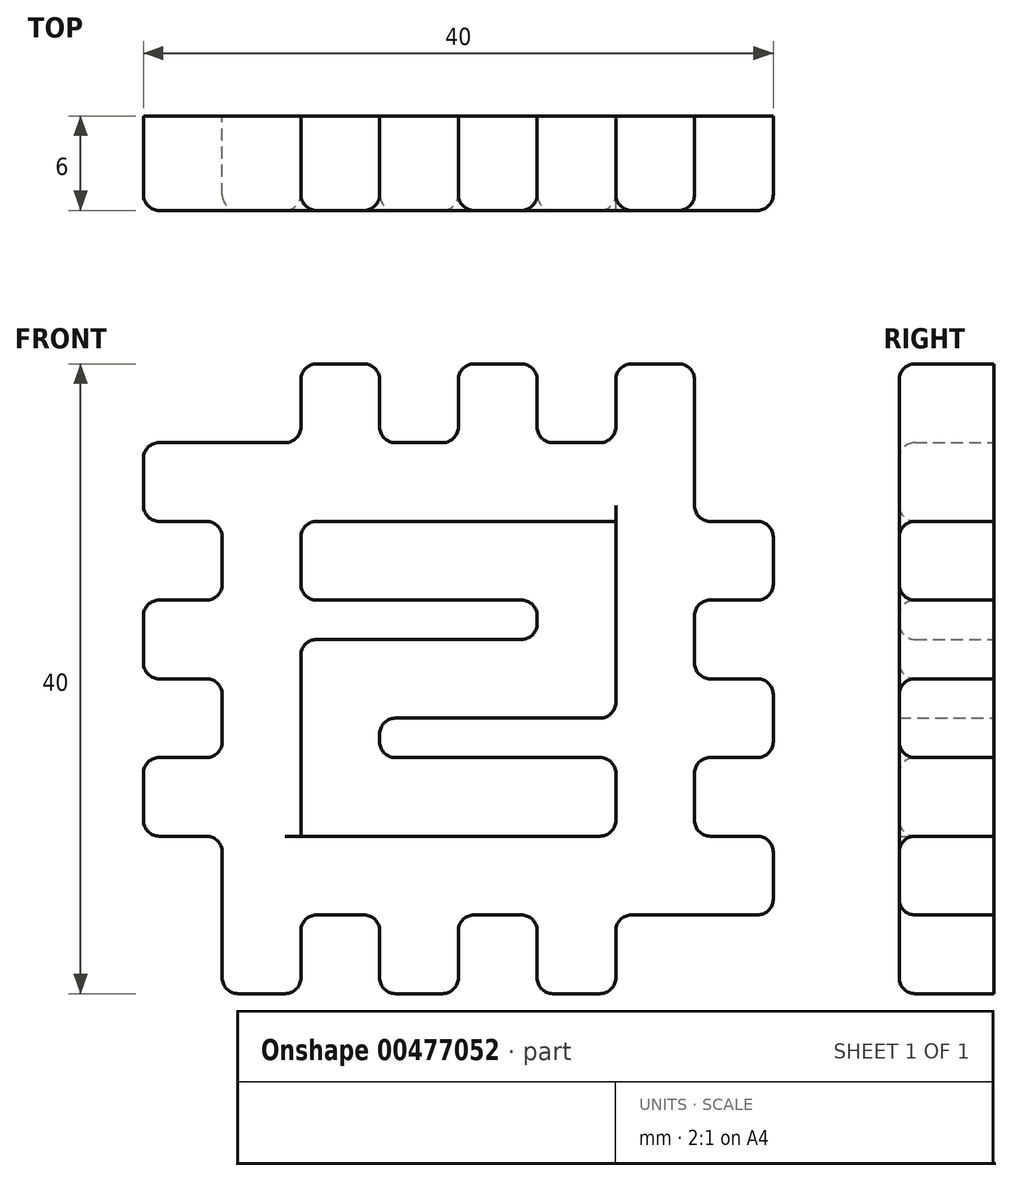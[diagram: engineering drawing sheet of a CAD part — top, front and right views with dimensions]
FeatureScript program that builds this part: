
annotation { "Feature Type Name" : "Feature", "Feature Type Description" : "" }
export const myFeature = defineFeature(function(context is Context, id is Id, definition is map)
    precondition{}
    {
        {
            var Q0;
            Q0=qCreatedBy(makeId("Front.planeOp"),FACE);
            var sketch = newSketch(context, id + "F0", { "sketchPlane" : qUnion([Q0])});
            skLineSegment(sketch, "E0.bottom", {"start": v(-15, -15) * mm, "end": v(15, -15) * mm});
            skLineSegment(sketch, "E0.top", {"start": v(-15, 15) * mm, "end": v(15, 15) * mm});
            skLineSegment(sketch, "E0.left", {"start": v(-15, -15) * mm, "end": v(-15, 15) * mm});
            skLineSegment(sketch, "E0.right", {"start": v(15, -15) * mm, "end": v(15, 15) * mm});
            skPoint(sketch, "E0.middle", {"position": v(0, 0) * mm});
            skLineSegment(sketch, "E1.bottom", {"start": v(-15, 15) * mm, "end": v(-20, 15) * mm});
            skLineSegment(sketch, "E1.top", {"start": v(-15, 10) * mm, "end": v(-20, 10) * mm});
            skLineSegment(sketch, "E1.left", {"start": v(-15, 15) * mm, "end": v(-15, 10) * mm});
            skLineSegment(sketch, "E1.right", {"start": v(-20, 15) * mm, "end": v(-20, 10) * mm});
            skPoint(sketch, "E2", {"position": v(-15, 0) * mm});
            skPoint(sketch, "E3", {"position": v(0, 15) * mm});
            skPoint(sketch, "E4", {"position": v(15, 0) * mm});
            skPoint(sketch, "E5", {"position": v(0, -15) * mm});
            skLineSegment(sketch, "E6.bottom", {"start": v(-15, 0) * mm, "end": v(-20, 0) * mm});
            skLineSegment(sketch, "E6.top", {"start": v(-15, 5) * mm, "end": v(-20, 5) * mm});
            skLineSegment(sketch, "E6.left", {"start": v(-15, 0) * mm, "end": v(-15, 5) * mm});
            skLineSegment(sketch, "E6.right", {"start": v(-20, 0) * mm, "end": v(-20, 5) * mm});
            skPoint(sketch, "E7", {"position": v(-15, -7.74) * mm});
            skPoint(sketch, "E8", {"position": v(-7.28, -15) * mm});
            skPoint(sketch, "E9", {"position": v(7.64, -15) * mm});
            skPoint(sketch, "E10", {"position": v(15, -7.4) * mm});
            skPoint(sketch, "E11", {"position": v(15, 8.08) * mm});
            skPoint(sketch, "E12", {"position": v(7.83, 15) * mm});
            skPoint(sketch, "E13", {"position": v(-7.7, 15) * mm});
            skPoint(sketch, "E14", {"position": v(-15, -5) * mm});
            skPoint(sketch, "E15", {"position": v(-15, -11.17) * mm});
            skPoint(sketch, "E16", {"position": v(-11.04, -15) * mm});
            skPoint(sketch, "E17", {"position": v(-3.27, -15) * mm});
            skPoint(sketch, "E18", {"position": v(5, -15) * mm});
            skPoint(sketch, "E19", {"position": v(11.4, -15) * mm});
            skPoint(sketch, "E20", {"position": v(15, -11.1) * mm});
            skPoint(sketch, "E21", {"position": v(15, -3.78) * mm});
            skPoint(sketch, "E22", {"position": v(15, 3.83) * mm});
            skPoint(sketch, "E23", {"position": v(15, 10) * mm});
            skPoint(sketch, "E24", {"position": v(11.09, 15) * mm});
            skPoint(sketch, "E25", {"position": v(4.04, 15) * mm});
            skPoint(sketch, "E26", {"position": v(-3.6, 15) * mm});
            skPoint(sketch, "E27", {"position": v(-11.54, 15) * mm});
            skLineSegment(sketch, "E28.bottom", {"start": v(-15, -5) * mm, "end": v(-20, -5) * mm});
            skLineSegment(sketch, "E28.top", {"start": v(-15, -10) * mm, "end": v(-20, -10) * mm});
            skLineSegment(sketch, "E28.left", {"start": v(-15, -5) * mm, "end": v(-15, -10) * mm});
            skLineSegment(sketch, "E28.right", {"start": v(-20, -5) * mm, "end": v(-20, -10) * mm});
            skLineSegment(sketch, "E29.bottom", {"start": v(15, 10) * mm, "end": v(20, 10) * mm});
            skLineSegment(sketch, "E29.top", {"start": v(15, 5) * mm, "end": v(20, 5) * mm});
            skLineSegment(sketch, "E29.left", {"start": v(15, 10) * mm, "end": v(15, 5) * mm});
            skLineSegment(sketch, "E29.right", {"start": v(20, 10) * mm, "end": v(20, 5) * mm});
            skLineSegment(sketch, "E30.bottom", {"start": v(15, 0) * mm, "end": v(20, 0) * mm});
            skLineSegment(sketch, "E30.top", {"start": v(15, -5) * mm, "end": v(20, -5) * mm});
            skLineSegment(sketch, "E30.left", {"start": v(15, 0) * mm, "end": v(15, -5) * mm});
            skLineSegment(sketch, "E30.right", {"start": v(20, 0) * mm, "end": v(20, -5) * mm});
            skLineSegment(sketch, "E31.bottom", {"start": v(15, -15) * mm, "end": v(20, -15) * mm});
            skLineSegment(sketch, "E31.top", {"start": v(15, -10) * mm, "end": v(20, -10) * mm});
            skLineSegment(sketch, "E31.left", {"start": v(15, -15) * mm, "end": v(15, -10) * mm});
            skLineSegment(sketch, "E31.right", {"start": v(20, -15) * mm, "end": v(20, -10) * mm});
            skLineSegment(sketch, "E32.bottom", {"start": v(-15, -15) * mm, "end": v(-10, -15) * mm});
            skLineSegment(sketch, "E32.top", {"start": v(-15, -20) * mm, "end": v(-10, -20) * mm});
            skLineSegment(sketch, "E32.left", {"start": v(-15, -15) * mm, "end": v(-15, -20) * mm});
            skLineSegment(sketch, "E32.right", {"start": v(-10, -15) * mm, "end": v(-10, -20) * mm});
            skLineSegment(sketch, "E33.bottom", {"start": v(0, -15) * mm, "end": v(-5, -15) * mm});
            skLineSegment(sketch, "E33.top", {"start": v(0, -20) * mm, "end": v(-5, -20) * mm});
            skLineSegment(sketch, "E33.left", {"start": v(0, -15) * mm, "end": v(0, -20) * mm});
            skLineSegment(sketch, "E33.right", {"start": v(-5, -15) * mm, "end": v(-5, -20) * mm});
            skLineSegment(sketch, "E34.bottom", {"start": v(5, -15) * mm, "end": v(10, -15) * mm});
            skLineSegment(sketch, "E34.top", {"start": v(5, -20) * mm, "end": v(10, -20) * mm});
            skLineSegment(sketch, "E34.left", {"start": v(5, -15) * mm, "end": v(5, -20) * mm});
            skLineSegment(sketch, "E34.right", {"start": v(10, -15) * mm, "end": v(10, -20) * mm});
            skLineSegment(sketch, "E35.bottom", {"start": v(-10, 15) * mm, "end": v(-5, 15) * mm});
            skLineSegment(sketch, "E35.top", {"start": v(-10, 20) * mm, "end": v(-5, 20) * mm});
            skLineSegment(sketch, "E35.left", {"start": v(-10, 15) * mm, "end": v(-10, 20) * mm});
            skLineSegment(sketch, "E35.right", {"start": v(-5, 15) * mm, "end": v(-5, 20) * mm});
            skLineSegment(sketch, "E36.bottom", {"start": v(0, 15) * mm, "end": v(5, 15) * mm});
            skLineSegment(sketch, "E36.top", {"start": v(0, 20) * mm, "end": v(5, 20) * mm});
            skLineSegment(sketch, "E36.left", {"start": v(0, 15) * mm, "end": v(0, 20) * mm});
            skLineSegment(sketch, "E36.right", {"start": v(5, 15) * mm, "end": v(5, 20) * mm});
            skLineSegment(sketch, "E37.bottom", {"start": v(15, 15) * mm, "end": v(10, 15) * mm});
            skLineSegment(sketch, "E37.top", {"start": v(15, 20) * mm, "end": v(10, 20) * mm});
            skLineSegment(sketch, "E37.left", {"start": v(15, 15) * mm, "end": v(15, 20) * mm});
            skLineSegment(sketch, "E37.right", {"start": v(10, 15) * mm, "end": v(10, 20) * mm});
            skLineSegment(sketch, "E38.bottom", {"start": v(-10, 10) * mm, "end": v(10, 10) * mm});
            skLineSegment(sketch, "E38.top", {"start": v(-10, 5) * mm, "end": v(10, 5) * mm});
            skLineSegment(sketch, "E38.left", {"start": v(-10, 10) * mm, "end": v(-10, 5) * mm});
            skLineSegment(sketch, "E38.right", {"start": v(10, 10) * mm, "end": v(10, 5) * mm});
            skLineSegment(sketch, "E39.bottom", {"start": v(10, 10) * mm, "end": v(5, 10) * mm});
            skLineSegment(sketch, "E39.top", {"start": v(10, 0) * mm, "end": v(5, 0) * mm});
            skLineSegment(sketch, "E39.left", {"start": v(10, 10) * mm, "end": v(10, 0) * mm});
            skLineSegment(sketch, "E39.right", {"start": v(5, 10) * mm, "end": v(5, 0) * mm});
            skLineSegment(sketch, "E40.bottom", {"start": v(10, 0) * mm, "end": v(-10, 0) * mm});
            skLineSegment(sketch, "E40.top", {"start": v(10, 0) * mm, "end": v(-10, 0) * mm});
            skLineSegment(sketch, "E40.left", {"start": v(10, 0) * mm, "end": v(10, 0) * mm});
            skLineSegment(sketch, "E40.right", {"start": v(-10, 0) * mm, "end": v(-10, 0) * mm});
            skLineSegment(sketch, "E41.bottom", {"start": v(-10, 0) * mm, "end": v(-5, 0) * mm});
            skLineSegment(sketch, "E41.top", {"start": v(-10, -10) * mm, "end": v(-5, -10) * mm});
            skLineSegment(sketch, "E41.left", {"start": v(-10, 0) * mm, "end": v(-10, -10) * mm});
            skLineSegment(sketch, "E41.right", {"start": v(-5, 0) * mm, "end": v(-5, -10) * mm});
            skLineSegment(sketch, "E42.bottom", {"start": v(-10, -10) * mm, "end": v(10, -10) * mm});
            skLineSegment(sketch, "E42.top", {"start": v(-10, -5) * mm, "end": v(10, -5) * mm});
            skLineSegment(sketch, "E42.left", {"start": v(-10, -10) * mm, "end": v(-10, -5) * mm});
            skLineSegment(sketch, "E42.right", {"start": v(10, -10) * mm, "end": v(10, -5) * mm});
            skLineSegment(sketch, "E43.bottom", {"start": v(-10, -2.5) * mm, "end": v(10, -2.5) * mm});
            skLineSegment(sketch, "E43.top", {"start": v(-10, 2.5) * mm, "end": v(10, 2.5) * mm});
            skLineSegment(sketch, "E43.left", {"start": v(-10, -2.5) * mm, "end": v(-10, 2.5) * mm});
            skLineSegment(sketch, "E43.right", {"start": v(10, -2.5) * mm, "end": v(10, 2.5) * mm});
            skSolve(sketch);
        }
        {
            var Q0;
            Q0 = qSketchRegion(id + "F0", true);
            extrude(context, id + "F1", {"entities" : qUnion([Q0]), "depth" : 6 * mm});
        }
        {
            var Q0;
            Q0=makeQuery(id+"F1.opExtrude","SWEPT_EDGE",EDGE,{"disambiguationData":[OSD([sQuery(id+"F0.wireOp",EDGE,"E38.bottom"),sQuery(id+"F0.wireOp",EDGE,"E38.left")])]});
            var Q1;
            Q1=makeQuery(id+"F1.opExtrude","SWEPT_EDGE",EDGE,{"disambiguationData":[OSD([sQuery(id+"F0.wireOp",EDGE,"E43.top"),sQuery(id+"F0.wireOp",EDGE,"E43.left")])]});
            var Q2;
            Q2=makeQuery(id+"F1.opExtrude","SWEPT_EDGE",EDGE,{"disambiguationData":[OSD([sQuery(id+"F0.wireOp",EDGE,"E39.right"),sQuery(id+"F0.wireOp",EDGE,"E43.top")])]});
            var Q3;
            Q3=makeQuery(id+"F1.opExtrude","SWEPT_EDGE",EDGE,{"disambiguationData":[OSD([sQuery(id+"F0.wireOp",EDGE,"E38.top"),sQuery(id+"F0.wireOp",EDGE,"E39.right")])]});
            var Q4;
            Q4=makeQuery(id+"F1.opExtrude","SWEPT_EDGE",EDGE,{"disambiguationData":[OSD([sQuery(id+"F0.wireOp",EDGE,"E31.top"),sQuery(id+"F0.wireOp",EDGE,"E31.right")])]});
            var Q5;
            Q5=makeQuery(id+"F1.opExtrude","SWEPT_EDGE",EDGE,{"disambiguationData":[OSD([sQuery(id+"F0.wireOp",EDGE,"E31.bottom"),sQuery(id+"F0.wireOp",EDGE,"E31.right")])]});
            var Q6;
            Q6=makeQuery(id+"F1.opExtrude","SWEPT_EDGE",EDGE,{"disambiguationData":[OSD([sQuery(id+"F0.wireOp",EDGE,"E0.bottom"),sQuery(id+"F0.wireOp",EDGE,"E34.bottom"),sQuery(id+"F0.wireOp",EDGE,"E34.right")])]});
            var Q7;
            Q7=makeQuery(id+"F1.opExtrude","SWEPT_EDGE",EDGE,{"disambiguationData":[OSD([sQuery(id+"F0.wireOp",EDGE,"E34.top"),sQuery(id+"F0.wireOp",EDGE,"E34.right")])]});
            var Q8;
            Q8=makeQuery(id+"F1.opExtrude","SWEPT_EDGE",EDGE,{"disambiguationData":[OSD([sQuery(id+"F0.wireOp",EDGE,"E34.top"),sQuery(id+"F0.wireOp",EDGE,"E34.left")])]});
            var Q9;
            Q9=makeQuery(id+"F1.opExtrude","SWEPT_EDGE",EDGE,{"disambiguationData":[OSD([sQuery(id+"F0.wireOp",EDGE,"E0.bottom"),sQuery(id+"F0.wireOp",EDGE,"E33.bottom"),sQuery(id+"F0.wireOp",EDGE,"E33.left")])]});
            var Q10;
            Q10=makeQuery(id+"F1.opExtrude","SWEPT_EDGE",EDGE,{"disambiguationData":[OSD([sQuery(id+"F0.wireOp",EDGE,"E33.top"),sQuery(id+"F0.wireOp",EDGE,"E33.left")])]});
            var Q11;
            Q11=makeQuery(id+"F1.opExtrude","SWEPT_EDGE",EDGE,{"disambiguationData":[OSD([sQuery(id+"F0.wireOp",EDGE,"E33.top"),sQuery(id+"F0.wireOp",EDGE,"E33.right")])]});
            var Q12;
            Q12=makeQuery(id+"F1.opExtrude","SWEPT_EDGE",EDGE,{"disambiguationData":[OSD([sQuery(id+"F0.wireOp",EDGE,"E0.bottom"),sQuery(id+"F0.wireOp",EDGE,"E32.bottom"),sQuery(id+"F0.wireOp",EDGE,"E32.right")])]});
            var Q13;
            Q13=makeQuery(id+"F1.opExtrude","SWEPT_EDGE",EDGE,{"disambiguationData":[OSD([sQuery(id+"F0.wireOp",EDGE,"E32.top"),sQuery(id+"F0.wireOp",EDGE,"E32.right")])]});
            var Q14;
            Q14=makeQuery(id+"F1.opExtrude","SWEPT_EDGE",EDGE,{"disambiguationData":[OSD([sQuery(id+"F0.wireOp",EDGE,"E32.top"),sQuery(id+"F0.wireOp",EDGE,"E32.left")])]});
            var Q15;
            Q15=makeQuery(id+"F1.opExtrude","SWEPT_EDGE",EDGE,{"disambiguationData":[OSD([sQuery(id+"F0.wireOp",EDGE,"E28.top"),sQuery(id+"F0.wireOp",EDGE,"E28.right")])]});
            var Q16;
            Q16=makeQuery(id+"F1.opExtrude","SWEPT_EDGE",EDGE,{"disambiguationData":[OSD([sQuery(id+"F0.wireOp",EDGE,"E6.bottom"),sQuery(id+"F0.wireOp",EDGE,"E6.right")])]});
            var Q17;
            Q17=makeQuery(id+"F1.opExtrude","SWEPT_EDGE",EDGE,{"disambiguationData":[OSD([sQuery(id+"F0.wireOp",EDGE,"E1.top"),sQuery(id+"F0.wireOp",EDGE,"E1.right")])]});
            var Q18;
            Q18=makeQuery(id+"F1.opExtrude","SWEPT_EDGE",EDGE,{"disambiguationData":[OSD([sQuery(id+"F0.wireOp",EDGE,"E30.top"),sQuery(id+"F0.wireOp",EDGE,"E30.right")])]});
            var Q19;
            Q19=makeQuery(id+"F1.opExtrude","SWEPT_EDGE",EDGE,{"disambiguationData":[OSD([sQuery(id+"F0.wireOp",EDGE,"E30.bottom"),sQuery(id+"F0.wireOp",EDGE,"E30.right")])]});
            var Q20;
            Q20=makeQuery(id+"F1.opExtrude","SWEPT_EDGE",EDGE,{"disambiguationData":[OSD([sQuery(id+"F0.wireOp",EDGE,"E29.top"),sQuery(id+"F0.wireOp",EDGE,"E29.right")])]});
            var Q21;
            Q21=makeQuery(id+"F1.opExtrude","SWEPT_EDGE",EDGE,{"disambiguationData":[OSD([sQuery(id+"F0.wireOp",EDGE,"E29.bottom"),sQuery(id+"F0.wireOp",EDGE,"E29.right")])]});
            var Q22;
            Q22=makeQuery(id+"F1.opExtrude","SWEPT_EDGE",EDGE,{"disambiguationData":[OSD([sQuery(id+"F0.wireOp",EDGE,"E42.bottom"),sQuery(id+"F0.wireOp",EDGE,"E42.left")])]});
            var Q23;
            Q23=makeQuery(id+"F1.opExtrude","SWEPT_EDGE",EDGE,{"disambiguationData":[OSD([sQuery(id+"F0.wireOp",EDGE,"E41.right"),sQuery(id+"F0.wireOp",EDGE,"E43.bottom")])]});
            var Q24;
            Q24=makeQuery(id+"F1.opExtrude","SWEPT_EDGE",EDGE,{"disambiguationData":[OSD([sQuery(id+"F0.wireOp",EDGE,"E37.top"),sQuery(id+"F0.wireOp",EDGE,"E37.left")])]});
            var Q25;
            Q25=makeQuery(id+"F1.opExtrude","SWEPT_EDGE",EDGE,{"disambiguationData":[OSD([sQuery(id+"F0.wireOp",EDGE,"E37.top"),sQuery(id+"F0.wireOp",EDGE,"E37.right")])]});
            var Q26;
            Q26=makeQuery(id+"F1.opExtrude","SWEPT_EDGE",EDGE,{"disambiguationData":[OSD([sQuery(id+"F0.wireOp",EDGE,"E0.top"),sQuery(id+"F0.wireOp",EDGE,"E36.bottom"),sQuery(id+"F0.wireOp",EDGE,"E36.right")])]});
            var Q27;
            Q27=makeQuery(id+"F1.opExtrude","SWEPT_EDGE",EDGE,{"disambiguationData":[OSD([sQuery(id+"F0.wireOp",EDGE,"E36.top"),sQuery(id+"F0.wireOp",EDGE,"E36.right")])]});
            var Q28;
            Q28=makeQuery(id+"F1.opExtrude","SWEPT_EDGE",EDGE,{"disambiguationData":[OSD([sQuery(id+"F0.wireOp",EDGE,"E36.top"),sQuery(id+"F0.wireOp",EDGE,"E36.left")])]});
            var Q29;
            Q29=makeQuery(id+"F1.opExtrude","SWEPT_EDGE",EDGE,{"disambiguationData":[OSD([sQuery(id+"F0.wireOp",EDGE,"E0.top"),sQuery(id+"F0.wireOp",EDGE,"E35.bottom"),sQuery(id+"F0.wireOp",EDGE,"E35.right")])]});
            var Q30;
            Q30=makeQuery(id+"F1.opExtrude","SWEPT_EDGE",EDGE,{"disambiguationData":[OSD([sQuery(id+"F0.wireOp",EDGE,"E35.top"),sQuery(id+"F0.wireOp",EDGE,"E35.right")])]});
            var Q31;
            Q31=makeQuery(id+"F1.opExtrude","SWEPT_EDGE",EDGE,{"disambiguationData":[OSD([sQuery(id+"F0.wireOp",EDGE,"E35.top"),sQuery(id+"F0.wireOp",EDGE,"E35.left")])]});
            var Q32;
            Q32=makeQuery(id+"F1.opExtrude","SWEPT_EDGE",EDGE,{"disambiguationData":[OSD([sQuery(id+"F0.wireOp",EDGE,"E42.bottom"),sQuery(id+"F0.wireOp",EDGE,"E42.right")])]});
            var Q33;
            Q33=makeQuery(id+"F1.opExtrude","SWEPT_EDGE",EDGE,{"disambiguationData":[OSD([sQuery(id+"F0.wireOp",EDGE,"E41.right"),sQuery(id+"F0.wireOp",EDGE,"E42.top")])]});
            var Q34;
            Q34=makeQuery(id+"F1.opExtrude","SWEPT_EDGE",EDGE,{"disambiguationData":[OSD([sQuery(id+"F0.wireOp",EDGE,"E43.bottom"),sQuery(id+"F0.wireOp",EDGE,"E43.right")])]});
            var Q35;
            Q35=makeQuery(id+"F1.opExtrude","SWEPT_EDGE",EDGE,{"disambiguationData":[OSD([sQuery(id+"F0.wireOp",EDGE,"E1.bottom"),sQuery(id+"F0.wireOp",EDGE,"E1.right")])]});
            var Q36;
            Q36=makeQuery(id+"F1.opExtrude","SWEPT_EDGE",EDGE,{"disambiguationData":[OSD([sQuery(id+"F0.wireOp",EDGE,"E0.top"),sQuery(id+"F0.wireOp",EDGE,"E37.bottom"),sQuery(id+"F0.wireOp",EDGE,"E37.right")])]});
            var Q37;
            Q37=makeQuery(id+"F1.opExtrude","SWEPT_EDGE",EDGE,{"disambiguationData":[OSD([sQuery(id+"F0.wireOp",EDGE,"E0.top"),sQuery(id+"F0.wireOp",EDGE,"E36.bottom"),sQuery(id+"F0.wireOp",EDGE,"E36.left")])]});
            var Q38;
            Q38=makeQuery(id+"F1.opExtrude","SWEPT_EDGE",EDGE,{"disambiguationData":[OSD([sQuery(id+"F0.wireOp",EDGE,"E0.left"),sQuery(id+"F0.wireOp",EDGE,"E6.top"),sQuery(id+"F0.wireOp",EDGE,"E6.left")])]});
            var Q39;
            Q39=makeQuery(id+"F1.opExtrude","SWEPT_EDGE",EDGE,{"disambiguationData":[OSD([sQuery(id+"F0.wireOp",EDGE,"E6.top"),sQuery(id+"F0.wireOp",EDGE,"E6.right")])]});
            var Q40;
            Q40=makeQuery(id+"F1.opExtrude","SWEPT_EDGE",EDGE,{"disambiguationData":[OSD([sQuery(id+"F0.wireOp",EDGE,"E0.left"),sQuery(id+"F0.wireOp",EDGE,"E28.bottom"),sQuery(id+"F0.wireOp",EDGE,"E28.left")])]});
            var Q41;
            Q41=makeQuery(id+"F1.opExtrude","SWEPT_EDGE",EDGE,{"disambiguationData":[OSD([sQuery(id+"F0.wireOp",EDGE,"E28.bottom"),sQuery(id+"F0.wireOp",EDGE,"E28.right")])]});
            var Q42;
            Q42=makeQuery(id+"F1.opExtrude","SWEPT_EDGE",EDGE,{"disambiguationData":[OSD([sQuery(id+"F0.wireOp",EDGE,"E0.bottom"),sQuery(id+"F0.wireOp",EDGE,"E34.bottom"),sQuery(id+"F0.wireOp",EDGE,"E34.left")])]});
            var Q43;
            Q43=makeQuery(id+"F1.opExtrude","SWEPT_EDGE",EDGE,{"disambiguationData":[OSD([sQuery(id+"F0.wireOp",EDGE,"E0.bottom"),sQuery(id+"F0.wireOp",EDGE,"E33.bottom"),sQuery(id+"F0.wireOp",EDGE,"E33.right")])]});
            var Q44;
            Q44=makeQuery(id+"F1.opExtrude","SWEPT_EDGE",EDGE,{"disambiguationData":[OSD([sQuery(id+"F0.wireOp",EDGE,"E0.left"),sQuery(id+"F0.wireOp",EDGE,"E28.top"),sQuery(id+"F0.wireOp",EDGE,"E28.left")])]});
            var Q45;
            Q45=makeQuery(id+"F1.opExtrude","SWEPT_EDGE",EDGE,{"disambiguationData":[OSD([sQuery(id+"F0.wireOp",EDGE,"E0.left"),sQuery(id+"F0.wireOp",EDGE,"E6.bottom"),sQuery(id+"F0.wireOp",EDGE,"E6.left")])]});
            var Q46;
            Q46=makeQuery(id+"F1.opExtrude","SWEPT_EDGE",EDGE,{"disambiguationData":[OSD([sQuery(id+"F0.wireOp",EDGE,"E0.left"),sQuery(id+"F0.wireOp",EDGE,"E1.top"),sQuery(id+"F0.wireOp",EDGE,"E1.left")])]});
            var Q47;
            Q47=makeQuery(id+"F1.opExtrude","SWEPT_EDGE",EDGE,{"disambiguationData":[OSD([sQuery(id+"F0.wireOp",EDGE,"E39.bottom"),sQuery(id+"F0.wireOp",EDGE,"E39.left")])]});
            var Q48;
            Q48=makeQuery(id+"F1.opExtrude","SWEPT_EDGE",EDGE,{"disambiguationData":[OSD([sQuery(id+"F0.wireOp",EDGE,"E42.top"),sQuery(id+"F0.wireOp",EDGE,"E42.right")])]});
            var Q49;
            Q49=makeQuery(id+"F1.opExtrude","SWEPT_EDGE",EDGE,{"disambiguationData":[OSD([sQuery(id+"F0.wireOp",EDGE,"E38.top"),sQuery(id+"F0.wireOp",EDGE,"E38.left")])]});
            var Q50;
            Q50=makeQuery(id+"F1.opExtrude","SWEPT_EDGE",EDGE,{"disambiguationData":[OSD([sQuery(id+"F0.wireOp",EDGE,"E0.top"),sQuery(id+"F0.wireOp",EDGE,"E35.bottom"),sQuery(id+"F0.wireOp",EDGE,"E35.left")])]});
            var Q51;
            Q51=makeQuery(id+"F1.opExtrude","SWEPT_EDGE",EDGE,{"disambiguationData":[OSD([sQuery(id+"F0.wireOp",EDGE,"E0.right"),sQuery(id+"F0.wireOp",EDGE,"E29.bottom"),sQuery(id+"F0.wireOp",EDGE,"E29.left")])]});
            var Q52;
            Q52=makeQuery(id+"F1.opExtrude","SWEPT_EDGE",EDGE,{"disambiguationData":[OSD([sQuery(id+"F0.wireOp",EDGE,"E0.right"),sQuery(id+"F0.wireOp",EDGE,"E30.bottom"),sQuery(id+"F0.wireOp",EDGE,"E30.left")])]});
            var Q53;
            Q53=makeQuery(id+"F1.opExtrude","SWEPT_EDGE",EDGE,{"disambiguationData":[OSD([sQuery(id+"F0.wireOp",EDGE,"E0.right"),sQuery(id+"F0.wireOp",EDGE,"E31.top"),sQuery(id+"F0.wireOp",EDGE,"E31.left")])]});
            var Q54;
            Q54=makeQuery(id+"F1.opExtrude","SWEPT_EDGE",EDGE,{"disambiguationData":[OSD([sQuery(id+"F0.wireOp",EDGE,"E0.right"),sQuery(id+"F0.wireOp",EDGE,"E30.top"),sQuery(id+"F0.wireOp",EDGE,"E30.left")])]});
            var Q55;
            Q55=makeQuery(id+"F1.opExtrude","SWEPT_EDGE",EDGE,{"disambiguationData":[OSD([sQuery(id+"F0.wireOp",EDGE,"E0.right"),sQuery(id+"F0.wireOp",EDGE,"E29.top"),sQuery(id+"F0.wireOp",EDGE,"E29.left")])]});
            fillet(context, id + "F2", {"entities" : qUnion([Q0, Q1, Q2, Q3, Q4, Q5, Q6, Q7, Q8, Q9, Q10, Q11, Q12, Q13, Q14, Q15, Q16, Q17, Q18, Q19, Q20, Q21, Q22, Q23, Q24, Q25, Q26, Q27, Q28, Q29, Q30, Q31, Q32, Q33, Q34, Q35, Q36, Q37, Q38, Q39, Q40, Q41, Q42, Q43, Q44, Q45, Q46, Q47, Q48, Q49, Q50, Q51, Q52, Q53, Q54, Q55]), "radius" : 1 * mm, "tangentPropagation" : true, "allowEdgeOverflow" : false});
        }
        {
            var Q0;
            Q0=makeQuery(id+"F1.opExtrude","CAP_EDGE",EDGE,{"disambiguationData":[OSD([sQuery(id+"F0.wireOp",EDGE,"E38.bottom"),sQuery(id+"F0.wireOp",EDGE,"E39.bottom")])],"isStart":false});
            fillet(context, id + "F3", {"entities" : qUnion([Q0]), "radius" : 1 * mm, "tangentPropagation" : true, "allowEdgeOverflow" : false});
        }
        {
            var Q0;
            Q0=makeQuery(id+"F1.opExtrude","CAP_EDGE",EDGE,{"disambiguationData":[OSD([sQuery(id+"F0.wireOp",EDGE,"E0.top"),sQuery(id+"F0.wireOp",EDGE,"E1.bottom")])],"isStart":false});
            fillet(context, id + "F4", {"entities" : qUnion([Q0]), "radius" : 1 * mm, "tangentPropagation" : true, "allowEdgeOverflow" : false});
        }
    });
